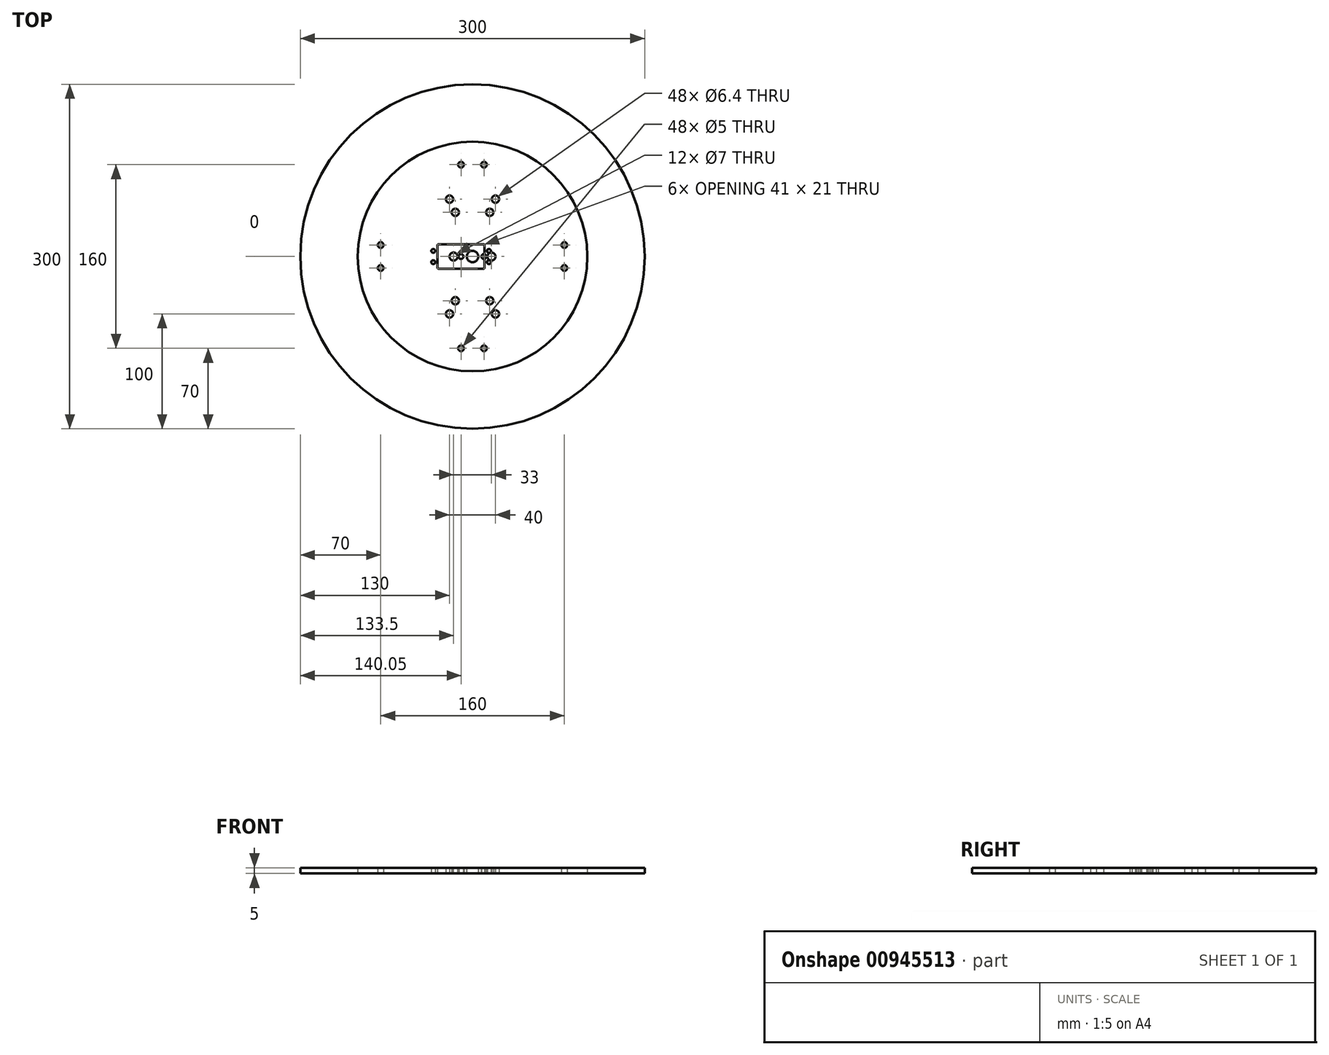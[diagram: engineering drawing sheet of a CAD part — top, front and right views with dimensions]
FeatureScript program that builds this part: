
annotation { "Feature Type Name" : "Feature", "Feature Type Description" : "" }
export const myFeature = defineFeature(function(context is Context, id is Id, definition is map)
    precondition{}
    {
        {
            var Q0;
            Q0=qCreatedBy(makeId("Top.planeOp"),FACE);
            var sketch = newSketch(context, id + "F0", { "sketchPlane" : qUnion([Q0])});
            skCircle(sketch, "E0", {"center": v(0, 0) * mm, "radius": 150 * mm});
            skSolve(sketch);
        }
        {
            var Q0;
            Q0 = qSketchRegion(id + "F0", true);
            extrude(context, id + "F1", {"entities" : qUnion([Q0]), "depth" : 5 * mm, "offsetDistance" : 25 * mm});
        }
        {
            var Q0;
            Q0=qCreatedBy(makeId("Top.planeOp"),FACE);
            var sketch = newSketch(context, id + "F2", { "sketchPlane" : qUnion([Q0])});
            skCircle(sketch, "E1", {"center": v(0, 0) * mm, "radius": 150 * mm});
            skCircle(sketch, "E2", {"center": v(0, 0) * mm, "radius": 5 * mm});
            skCircle(sketch, "E3", {"center": v(15, 38.5) * mm, "radius": 3.2 * mm});
            skCircle(sketch, "E4", {"center": v(-15, 38.5) * mm, "radius": 3.2 * mm});
            skCircle(sketch, "E5.MirrorC", {"center": v(15, -38.5) * mm, "radius": 3.2 * mm});
            skCircle(sketch, "E6.MirrorC", {"center": v(-15, -38.5) * mm, "radius": 3.2 * mm});
            skCircle(sketch, "E7", {"center": v(10, -80) * mm, "radius": 2.5 * mm});
            skCircle(sketch, "E8", {"center": v(-10, -80) * mm, "radius": 2.5 * mm});
            skCircle(sketch, "E9.MirrorC", {"center": v(10, 80) * mm, "radius": 2.5 * mm});
            skCircle(sketch, "E10.MirrorC", {"center": v(-10, 80) * mm, "radius": 2.5 * mm});
            skCircle(sketch, "E11", {"center": v(80, 10) * mm, "radius": 2.5 * mm});
            skCircle(sketch, "E12", {"center": v(80, -10) * mm, "radius": 2.5 * mm});
            skCircle(sketch, "E13.MirrorC", {"center": v(-80, 10) * mm, "radius": 2.5 * mm});
            skCircle(sketch, "E14.MirrorC", {"center": v(-80, -10) * mm, "radius": 2.5 * mm});
            skCircle(sketch, "E15", {"center": v(-10, 0) * mm, "radius": 2.15 * mm});
            skCircle(sketch, "E16", {"center": v(-16.5, 0) * mm, "radius": 3.5 * mm});
            skCircle(sketch, "E17.MirrorC", {"center": v(10, 0) * mm, "radius": 2.15 * mm});
            skCircle(sketch, "E18.MirrorC", {"center": v(16.5, 0) * mm, "radius": 3.5 * mm});
            skSolve(sketch);
        }
        {
            var Q0;
            Q0 = qSketchRegion(id + "F2", true);
            extrude(context, id + "F3", {"entities" : qUnion([Q0]), "depth" : 5 * mm, "offsetDistance" : 25 * mm});
        }
        {
            var Q0;
            Q0=qCreatedBy(makeId("Top.planeOp"),FACE);
            var sketch = newSketch(context, id + "F4", { "sketchPlane" : qUnion([Q0])});
            skCircle(sketch, "E19", {"center": v(0, 0) * mm, "radius": 100 * mm});
            skCircle(sketch, "E20", {"center": v(20, 50) * mm, "radius": 3.2 * mm});
            skCircle(sketch, "E21.MirrorC", {"center": v(-20, 50) * mm, "radius": 3.2 * mm});
            skCircle(sketch, "E22.MirrorC", {"center": v(-20, -50) * mm, "radius": 3.2 * mm});
            skCircle(sketch, "E23.MirrorC", {"center": v(20, -50) * mm, "radius": 3.2 * mm});
            skLineSegment(sketch, "E24.bottom", {"start": v(-30.45, 10.5) * mm, "end": v(10.55, 10.5) * mm});
            skLineSegment(sketch, "E24.top", {"start": v(-30.45, -10.5) * mm, "end": v(10.55, -10.5) * mm});
            skLineSegment(sketch, "E24.left", {"start": v(-30.45, 10.5) * mm, "end": v(-30.45, -10.5) * mm});
            skLineSegment(sketch, "E24.right", {"start": v(10.55, 10.5) * mm, "end": v(10.55, -10.5) * mm});
            skCircle(sketch, "E25", {"center": v(14.3, 4.9) * mm, "radius": 1.7 * mm});
            skLineSegment(sketch, "E26", {"start": v(-9.95, 10.5) * mm, "end": v(-9.95, -10.5) * mm});
            skCircle(sketch, "E27.MirrorC", {"center": v(-34.2, 4.9) * mm, "radius": 1.7 * mm});
            skCircle(sketch, "E28.MirrorC", {"center": v(-34.2, -4.9) * mm, "radius": 1.7 * mm});
            skCircle(sketch, "E29.MirrorC", {"center": v(14.3, -4.9) * mm, "radius": 1.7 * mm});
            skLineSegment(sketch, "E30.left", {"start": v(-30.45, 1.5) * mm, "end": v(-30.45, -1.5) * mm});
            skLineSegment(sketch, "E31.MirrorCS", {"start": v(10.55, 1.5) * mm, "end": v(10.55, -1.5) * mm});
            skSolve(sketch);
        }
        {
            var Q0;
            Q0=makeQuery(id+"F4.imprint","IMPRINT",FACE,{"disambiguationData":[TD([[makeQuery(id+"F4.imprint","IMPRINT",EDGE,{"derivedFrom":sQuery(id+"F4.wireOp",EDGE,"E19")}),1.0]])]});
            extrude(context, id + "F5", {"entities" : qUnion([Q0]), "depth" : 5 * mm, "offsetDistance" : 25 * mm});
        }
        {
            var Q0;
            Q0=makeQuery(id+"F5.opExtrude","SWEPT_EDGE",EDGE,{"disambiguationData":[OSD([sQuery(id+"F4.wireOp",EDGE,"E24.bottom"),sQuery(id+"F4.wireOp",EDGE,"E24.left")])]});
            var Q1;
            Q1=makeQuery(id+"F5.opExtrude","SWEPT_EDGE",EDGE,{"disambiguationData":[OSD([sQuery(id+"F4.wireOp",EDGE,"E24.top"),sQuery(id+"F4.wireOp",EDGE,"E24.left")])]});
            var Q2;
            Q2=makeQuery(id+"F5.opExtrude","SWEPT_EDGE",EDGE,{"disambiguationData":[OSD([sQuery(id+"F4.wireOp",EDGE,"E24.top"),sQuery(id+"F4.wireOp",EDGE,"E24.right")])]});
            var Q3;
            Q3=makeQuery(id+"F5.opExtrude","SWEPT_EDGE",EDGE,{"disambiguationData":[OSD([sQuery(id+"F4.wireOp",EDGE,"E24.bottom"),sQuery(id+"F4.wireOp",EDGE,"E24.right")])]});
            fillet(context, id + "F6", {"entities" : qUnion([Q0, Q1, Q2, Q3]), "radius" : 0.5 * mm, "tangentPropagation" : true, "allowEdgeOverflow" : false});
        }
    });
